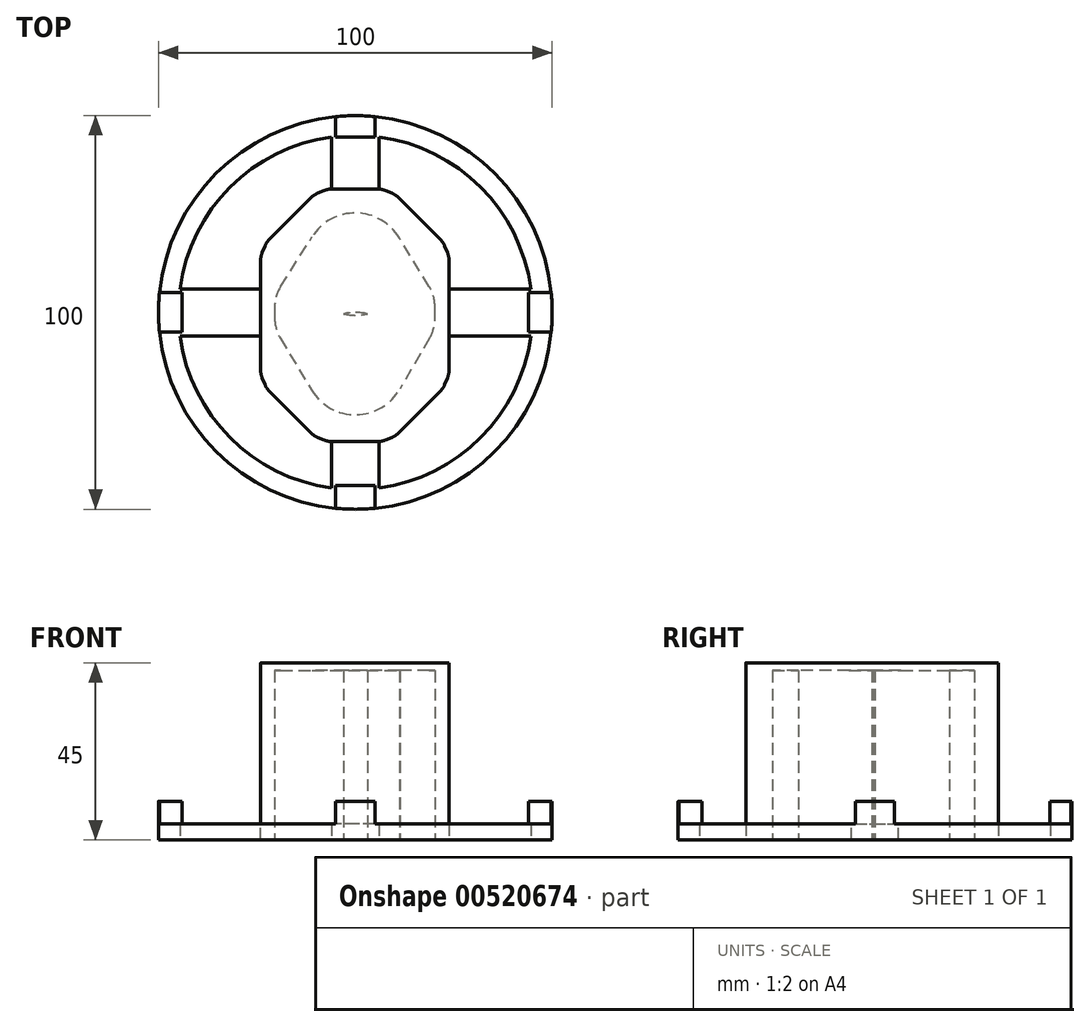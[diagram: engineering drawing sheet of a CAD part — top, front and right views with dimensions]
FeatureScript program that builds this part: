
annotation { "Feature Type Name" : "Feature", "Feature Type Description" : "" }
export const myFeature = defineFeature(function(context is Context, id is Id, definition is map)
    precondition{}
    {
        {
            var Q0;
            Q0=qCreatedBy(makeId("Top.planeOp"),FACE);
            var sketch = newSketch(context, id + "F0", { "sketchPlane" : qUnion([Q0])});
            skCircle(sketch, "E0", {"center": v(0, 0) * mm, "radius": 50 * mm});
            skSolve(sketch);
        }
        {
            var Q0;
            Q0=qSketchRegion(id+"F0",true);
            extrude(context, id + "F1", {"entities" : qUnion([Q0]), "depth" : 4 * mm, "offsetDistance" : 25 * mm});
        }
        {
            var Q0;
            Q0=makeQuery(id+"F1.opExtrude","CAP_FACE",FACE,{"disambiguationData":[OSD([sQuery(id+"F0.wireOp",EDGE,"E0")])],"isStart":false});
            var sketch = newSketch(context, id + "F2", { "sketchPlane" : qUnion([Q0])});
            skLineSegment(sketch, "E1.bottom", {"start": v(5, 50) * mm, "end": v(-5, 50) * mm});
            skLineSegment(sketch, "E1.top", {"start": v(5, 44.5) * mm, "end": v(-5, 44.5) * mm});
            skLineSegment(sketch, "E1.left", {"start": v(5, 50) * mm, "end": v(5, 44.5) * mm});
            skLineSegment(sketch, "E1.right", {"start": v(-5, 50) * mm, "end": v(-5, 44.5) * mm});
            skLineSegment(sketch, "E2.bottom", {"start": v(5, -44) * mm, "end": v(-5, -44) * mm});
            skLineSegment(sketch, "E2.top", {"start": v(5, -50) * mm, "end": v(-5, -50) * mm});
            skLineSegment(sketch, "E2.left", {"start": v(5, -44) * mm, "end": v(5, -50) * mm});
            skLineSegment(sketch, "E2.right", {"start": v(-5, -44) * mm, "end": v(-5, -50) * mm});
            skLineSegment(sketch, "E3.bottom", {"start": v(-44, 5) * mm, "end": v(-44, -5) * mm});
            skLineSegment(sketch, "E3.top", {"start": v(-50, 5) * mm, "end": v(-50, -5) * mm});
            skLineSegment(sketch, "E3.left", {"start": v(-50, 5) * mm, "end": v(-44, 5) * mm});
            skLineSegment(sketch, "E3.right", {"start": v(-50, -5) * mm, "end": v(-44, -5) * mm});
            skLineSegment(sketch, "E4.bottom", {"start": v(50, -5) * mm, "end": v(50, 5) * mm});
            skLineSegment(sketch, "E4.top", {"start": v(44, -5) * mm, "end": v(44, 5) * mm});
            skLineSegment(sketch, "E4.left", {"start": v(50, -5) * mm, "end": v(44, -5) * mm});
            skLineSegment(sketch, "E4.right", {"start": v(50, 5) * mm, "end": v(44, 5) * mm});
            skSolve(sketch);
        }
        {
            var Q0;
            {var subQ4=sQuery(id+"F2.wireOp",EDGE,"E1.top");Q0=makeQuery(id+"F2.imprint","IMPRINT",FACE,{"disambiguationData":[TD([[makeQuery(id+"F2.imprint","IMPRINT",EDGE,{"derivedFrom":subQ4}),-1.0]])]});}
            extrude(context, id + "F3", {"entities" : qUnion([Q0]), "operationType" : NewBodyOperationType.ADD, "depth" : 5.8 * mm, "offsetDistance" : 25 * mm});
        }
        {
            var Q0;
            {var subQ5=sQuery(id+"F2.wireOp",EDGE,"E2.bottom");Q0=makeQuery(id+"F2.imprint","IMPRINT",FACE,{"disambiguationData":[TD([[makeQuery(id+"F2.imprint","IMPRINT",EDGE,{"derivedFrom":subQ5}),1.0]])]});}
            extrude(context, id + "F4", {"entities" : qUnion([Q0]), "operationType" : NewBodyOperationType.ADD, "depth" : 5.8 * mm, "offsetDistance" : 25 * mm});
        }
        {
            var Q0;
            {var subQ5=sQuery(id+"F2.wireOp",EDGE,"E3.bottom");Q0=makeQuery(id+"F2.imprint","IMPRINT",FACE,{"disambiguationData":[TD([[makeQuery(id+"F2.imprint","IMPRINT",EDGE,{"derivedFrom":subQ5}),-1.0]])]});}
            var Q1;
            {var subQ1=sQuery(id+"F2.wireOp",EDGE,"E4.top");Q1=makeQuery(id+"F2.imprint","IMPRINT",FACE,{"disambiguationData":[TD([[makeQuery(id+"F2.imprint","IMPRINT",EDGE,{"derivedFrom":subQ1}),-1.0]])]});}
            extrude(context, id + "F5", {"entities" : qUnion([Q0, Q1]), "operationType" : NewBodyOperationType.ADD, "depth" : 5.8 * mm, "offsetDistance" : 25 * mm});
        }
        {
            var Q0;
            Q0=qCreatedBy(makeId("Top.planeOp"),FACE);
            var sketch = newSketch(context, id + "F6", { "sketchPlane" : qUnion([Q0])});
            skCircle(sketch, "E5", {"center": v(0, 0) * mm, "radius": 45 * mm});
            skSolve(sketch);
        }
        {
            var Q0;
            Q0=qSketchRegion(id+"F6",true);
            extrude(context, id + "F7", {"entities" : qUnion([Q0]), "operationType" : NewBodyOperationType.REMOVE, "depth" : 4 * mm, "offsetDistance" : 25 * mm});
        }
        {
            var Q0;
            Q0=qCreatedBy(makeId("Top.planeOp"),FACE);
            var sketch = newSketch(context, id + "F8", { "sketchPlane" : qUnion([Q0])});
            skLineSegment(sketch, "E6.bottom", {"start": v(-6, 46.88) * mm, "end": v(6, 46.88) * mm});
            skLineSegment(sketch, "E6.top", {"start": v(-6, 0) * mm, "end": v(6, 0) * mm});
            skLineSegment(sketch, "E6.left", {"start": v(-6, 46.88) * mm, "end": v(-6, 0) * mm});
            skLineSegment(sketch, "E6.right", {"start": v(6, 46.88) * mm, "end": v(6, 0) * mm});
            skLineSegment(sketch, "E7.top", {"start": v(-6, -46.78) * mm, "end": v(6, -46.78) * mm});
            skLineSegment(sketch, "E7.left", {"start": v(-6, 0) * mm, "end": v(-6, -46.78) * mm});
            skLineSegment(sketch, "E7.right", {"start": v(6, 0) * mm, "end": v(6, -46.78) * mm});
            skLineSegment(sketch, "E8.bottom", {"start": v(0, -6) * mm, "end": v(46.83, -6) * mm});
            skLineSegment(sketch, "E8.top", {"start": v(0, 6) * mm, "end": v(46.83, 6) * mm});
            skLineSegment(sketch, "E8.left", {"start": v(0, -6) * mm, "end": v(0, 6) * mm});
            skLineSegment(sketch, "E8.right", {"start": v(46.83, -6) * mm, "end": v(46.83, 6) * mm});
            skLineSegment(sketch, "E9.bottom", {"start": v(0, 6) * mm, "end": v(-46.57, 6) * mm});
            skLineSegment(sketch, "E9.top", {"start": v(0, -6) * mm, "end": v(-46.57, -6) * mm});
            skLineSegment(sketch, "E9.left", {"start": v(0, 6) * mm, "end": v(0, -6) * mm});
            skLineSegment(sketch, "E9.right", {"start": v(-46.57, 6) * mm, "end": v(-46.57, -6) * mm});
            skSolve(sketch);
        }
        {
            var Q0;
            Q0=qSketchRegion(id+"F8",true);
            extrude(context, id + "F9", {"entities" : qUnion([Q0]), "operationType" : NewBodyOperationType.ADD, "depth" : 4 * mm, "offsetDistance" : 25 * mm});
        }
        {
            var Q0;
            Q0=makeQuery(id+"FJTa6KurGkZYtoZ_1.boolean.opBoolean","MERGE",FACE,{"derivedFrom":[makeQuery(id+"F9.boolean.opBoolean","MERGE",FACE,{"derivedFrom":[makeQuery(id+"F1.opExtrude","CAP_FACE",FACE,{"disambiguationData":[OSD([sQuery(id+"F0.wireOp",EDGE,"E0")])],"isStart":true}),makeQuery(id+"F9.opExtrude","CAP_FACE",FACE,{"disambiguationData":[OSD([sQuery(id+"F8.wireOp",EDGE,"E6.bottom"),sQuery(id+"F8.wireOp",EDGE,"E6.left"),sQuery(id+"F8.wireOp",EDGE,"E6.right"),sQuery(id+"F8.wireOp",EDGE,"E7.top"),sQuery(id+"F8.wireOp",EDGE,"E7.left"),sQuery(id+"F8.wireOp",EDGE,"E7.right"),sQuery(id+"F8.wireOp",EDGE,"E8.bottom"),sQuery(id+"F8.wireOp",EDGE,"E8.top"),sQuery(id+"F8.wireOp",EDGE,"E8.right"),sQuery(id+"F8.wireOp",EDGE,"E9.bottom"),sQuery(id+"F8.wireOp",EDGE,"E9.top"),sQuery(id+"F8.wireOp",EDGE,"E9.right")])],"isStart":true})]}),makeQuery(id+"FJTa6KurGkZYtoZ_1.opExtrude","CAP_FACE",FACE,{"disambiguationData":[OSD([sQuery(id+"FEZX3pMElbrMIAv_1.wireOp",EDGE,"CWDysEy2-1OXt-7EfP-3vaQ-WOueIKtrEB2b")])],"isStart":true})]});
            var sketch = newSketch(context, id + "F10", { "sketchPlane" : qUnion([Q0])});
            skCircle(sketch, "E10", {"center": v(0, 0) * mm, "radius": 22.5 * mm});
            skSolve(sketch);
        }
        {
            var Q0;
            Q0=qSketchRegion(id+"F10",true);
            extrude(context, id + "F11", {"entities" : qUnion([Q0]), "operationType" : NewBodyOperationType.REMOVE, "oppositeDirection" : true, "depth" : 25 * mm, "offsetDistance" : 25 * mm});
        }
        {
            var Q0;
            Q0=qCreatedBy(makeId("Top.planeOp"),FACE);
            var sketch = newSketch(context, id + "F12", { "sketchPlane" : qUnion([Q0])});
            skLineSegment(sketch, "E11.bottom", {"start": v(-24.06, 31.35) * mm, "end": v(23.77, 31.35) * mm});
            skLineSegment(sketch, "E11.top", {"start": v(-24.06, -32.81) * mm, "end": v(23.77, -32.81) * mm});
            skLineSegment(sketch, "E11.left", {"start": v(-24.06, 31.35) * mm, "end": v(-24.06, -32.81) * mm});
            skLineSegment(sketch, "E11.right", {"start": v(23.77, 31.35) * mm, "end": v(23.77, -32.81) * mm});
            skSolve(sketch);
        }
        {
            var Q0;
            Q0 = qSketchRegion(id + "F12", true);
            extrude(context, id + "F13", {"entities" : qUnion([Q0]), "operationType" : NewBodyOperationType.ADD, "depth" : 45 * mm, "offsetDistance" : 25 * mm});
        }
        {
            var Q0;
            Q0=makeQuery(id+"F13.opExtrude","SWEPT_EDGE",EDGE,{"disambiguationData":[OSD([sQuery(id+"F12.wireOp",EDGE,"E11.bottom"),sQuery(id+"F12.wireOp",EDGE,"E11.left")])]});
            var Q1;
            Q1=makeQuery(id+"F13.opExtrude","SWEPT_EDGE",EDGE,{"disambiguationData":[OSD([sQuery(id+"F12.wireOp",EDGE,"E11.bottom"),sQuery(id+"F12.wireOp",EDGE,"E11.right")])]});
            var Q2;
            Q2=makeQuery(id+"F13.opExtrude","SWEPT_EDGE",EDGE,{"disambiguationData":[OSD([sQuery(id+"F12.wireOp",EDGE,"E11.top"),sQuery(id+"F12.wireOp",EDGE,"E11.right")])]});
            var Q3;
            Q3=makeQuery(id+"F13.opExtrude","SWEPT_EDGE",EDGE,{"disambiguationData":[OSD([sQuery(id+"F12.wireOp",EDGE,"E11.top"),sQuery(id+"F12.wireOp",EDGE,"E11.left")])]});
            chamfer(context, id + "F14", {"entities" : qUnion([Q0, Q1, Q2, Q3]), "width" : 15 * mm, "tangentPropagation" : true});
        }
        {
            var Q0;
            {var subQ0=sQuery(id+"F12.wireOp",EDGE,"E11.bottom");Q0=makeQuery(id+"F14.opChamfer","BLEND_EDGE",EDGE,{"blendedFrom":[makeQuery(id+"F13.opExtrude","SWEPT_EDGE",EDGE,{"disambiguationData":[OSD([subQ0,sQuery(id+"F12.wireOp",EDGE,"E11.left")])]}),makeQuery(id+"F13.opExtrude","SWEPT_FACE",FACE,{"disambiguationData":[OSD([subQ0])]})],"blendedInto":[makeQuery(id+"F13.opExtrude","SWEPT_FACE",FACE,{"disambiguationData":[OSD([subQ0])]})]});}
            var Q1;
            {var subQ0=sQuery(id+"F12.wireOp",EDGE,"E11.bottom");Q1=makeQuery(id+"F14.opChamfer","BLEND_EDGE",EDGE,{"blendedFrom":[makeQuery(id+"F13.opExtrude","SWEPT_EDGE",EDGE,{"disambiguationData":[OSD([subQ0,sQuery(id+"F12.wireOp",EDGE,"E11.right")])]}),makeQuery(id+"F13.opExtrude","SWEPT_FACE",FACE,{"disambiguationData":[OSD([subQ0])]})],"blendedInto":[makeQuery(id+"F13.opExtrude","SWEPT_FACE",FACE,{"disambiguationData":[OSD([subQ0])]})]});}
            var Q2;
            {var subQ0=sQuery(id+"F12.wireOp",EDGE,"E11.left");Q2=makeQuery(id+"F14.opChamfer","BLEND_EDGE",EDGE,{"blendedFrom":[makeQuery(id+"F13.opExtrude","SWEPT_EDGE",EDGE,{"disambiguationData":[OSD([sQuery(id+"F12.wireOp",EDGE,"E11.top"),subQ0])]}),makeQuery(id+"F13.opExtrude","SWEPT_FACE",FACE,{"disambiguationData":[OSD([subQ0])]})],"blendedInto":[makeQuery(id+"F13.opExtrude","SWEPT_FACE",FACE,{"disambiguationData":[OSD([subQ0])]})]});}
            var Q3;
            {var subQ0=sQuery(id+"F12.wireOp",EDGE,"E11.top");Q3=makeQuery(id+"F14.opChamfer","BLEND_EDGE",EDGE,{"blendedFrom":[makeQuery(id+"F13.opExtrude","SWEPT_EDGE",EDGE,{"disambiguationData":[OSD([subQ0,sQuery(id+"F12.wireOp",EDGE,"E11.left")])]}),makeQuery(id+"F13.opExtrude","SWEPT_FACE",FACE,{"disambiguationData":[OSD([subQ0])]})],"blendedInto":[makeQuery(id+"F13.opExtrude","SWEPT_FACE",FACE,{"disambiguationData":[OSD([subQ0])]})]});}
            var Q4;
            {var subQ0=sQuery(id+"F12.wireOp",EDGE,"E11.top");Q4=makeQuery(id+"F14.opChamfer","BLEND_EDGE",EDGE,{"blendedFrom":[makeQuery(id+"F13.opExtrude","SWEPT_EDGE",EDGE,{"disambiguationData":[OSD([subQ0,sQuery(id+"F12.wireOp",EDGE,"E11.right")])]}),makeQuery(id+"F13.opExtrude","SWEPT_FACE",FACE,{"disambiguationData":[OSD([subQ0])]})],"blendedInto":[makeQuery(id+"F13.opExtrude","SWEPT_FACE",FACE,{"disambiguationData":[OSD([subQ0])]})]});}
            var Q5;
            {var subQ0=sQuery(id+"F12.wireOp",EDGE,"E11.right");Q5=makeQuery(id+"F14.opChamfer","BLEND_EDGE",EDGE,{"blendedFrom":[makeQuery(id+"F13.opExtrude","SWEPT_EDGE",EDGE,{"disambiguationData":[OSD([sQuery(id+"F12.wireOp",EDGE,"E11.top"),subQ0])]}),makeQuery(id+"F13.opExtrude","SWEPT_FACE",FACE,{"disambiguationData":[OSD([subQ0])]})],"blendedInto":[makeQuery(id+"F13.opExtrude","SWEPT_FACE",FACE,{"disambiguationData":[OSD([subQ0])]})]});}
            var Q6;
            {var subQ0=sQuery(id+"F12.wireOp",EDGE,"E11.right");Q6=makeQuery(id+"F14.opChamfer","BLEND_EDGE",EDGE,{"blendedFrom":[makeQuery(id+"F13.opExtrude","SWEPT_EDGE",EDGE,{"disambiguationData":[OSD([sQuery(id+"F12.wireOp",EDGE,"E11.bottom"),subQ0])]}),makeQuery(id+"F13.opExtrude","SWEPT_FACE",FACE,{"disambiguationData":[OSD([subQ0])]})],"blendedInto":[makeQuery(id+"F13.opExtrude","SWEPT_FACE",FACE,{"disambiguationData":[OSD([subQ0])]})]});}
            var Q7;
            {var subQ0=sQuery(id+"F12.wireOp",EDGE,"E11.left");Q7=makeQuery(id+"F14.opChamfer","BLEND_EDGE",EDGE,{"blendedFrom":[makeQuery(id+"F13.opExtrude","SWEPT_EDGE",EDGE,{"disambiguationData":[OSD([sQuery(id+"F12.wireOp",EDGE,"E11.bottom"),subQ0])]}),makeQuery(id+"F13.opExtrude","SWEPT_FACE",FACE,{"disambiguationData":[OSD([subQ0])]})],"blendedInto":[makeQuery(id+"F13.opExtrude","SWEPT_FACE",FACE,{"disambiguationData":[OSD([subQ0])]})]});}
            chamfer(context, id + "F15", {"entities" : qUnion([Q0, Q1, Q2, Q3, Q4, Q5, Q6, Q7]), "width" : 5 * mm, "tangentPropagation" : true});
        }
        {
            var Q0;
            {var subQ0=sQuery(id+"F12.wireOp",EDGE,"E11.left");var subQ1=makeQuery(id+"F13.opExtrude","SWEPT_FACE",FACE,{"disambiguationData":[OSD([subQ0])]});Q0=makeQuery(id+"F15.opChamfer","BLEND_EDGE",EDGE,{"blendedFrom":[makeQuery(id+"F14.opChamfer","BLEND_EDGE",EDGE,{"blendedFrom":[makeQuery(id+"F13.opExtrude","SWEPT_EDGE",EDGE,{"disambiguationData":[OSD([sQuery(id+"F12.wireOp",EDGE,"E11.bottom"),subQ0])]}),subQ1],"blendedInto":[subQ1]}),subQ1],"blendedInto":[subQ1]});}
            var Q1;
            {var subQ0=sQuery(id+"F12.wireOp",EDGE,"E11.left");var subQ1=sQuery(id+"F12.wireOp",EDGE,"E11.bottom");Q1=makeQuery(id+"F15.opChamfer","BLEND_EDGE",EDGE,{"blendedFrom":[makeQuery(id+"F14.opChamfer","BLEND_EDGE",EDGE,{"blendedFrom":[makeQuery(id+"F13.opExtrude","SWEPT_EDGE",EDGE,{"disambiguationData":[OSD([subQ1,subQ0])]}),makeQuery(id+"F13.opExtrude","SWEPT_FACE",FACE,{"disambiguationData":[OSD([subQ0])]})],"blendedInto":[makeQuery(id+"F13.opExtrude","SWEPT_FACE",FACE,{"disambiguationData":[OSD([subQ0])]})]}),makeQuery(id+"F14.opChamfer","BLEND_FACE",FACE,{"disambiguationData":[OSD([subQ1,subQ0])]})],"blendedInto":[makeQuery(id+"F14.opChamfer","BLEND_FACE",FACE,{"disambiguationData":[OSD([subQ1,subQ0])]})]});}
            var Q2;
            {var subQ0=sQuery(id+"F12.wireOp",EDGE,"E11.left");var subQ1=sQuery(id+"F12.wireOp",EDGE,"E11.bottom");Q2=makeQuery(id+"F15.opChamfer","BLEND_EDGE",EDGE,{"blendedFrom":[makeQuery(id+"F14.opChamfer","BLEND_EDGE",EDGE,{"blendedFrom":[makeQuery(id+"F13.opExtrude","SWEPT_EDGE",EDGE,{"disambiguationData":[OSD([subQ1,subQ0])]}),makeQuery(id+"F13.opExtrude","SWEPT_FACE",FACE,{"disambiguationData":[OSD([subQ1])]})],"blendedInto":[makeQuery(id+"F13.opExtrude","SWEPT_FACE",FACE,{"disambiguationData":[OSD([subQ1])]})]}),makeQuery(id+"F14.opChamfer","BLEND_FACE",FACE,{"disambiguationData":[OSD([subQ1,subQ0])]})],"blendedInto":[makeQuery(id+"F14.opChamfer","BLEND_FACE",FACE,{"disambiguationData":[OSD([subQ1,subQ0])]})]});}
            var Q3;
            {var subQ0=sQuery(id+"F12.wireOp",EDGE,"E11.bottom");var subQ1=makeQuery(id+"F13.opExtrude","SWEPT_FACE",FACE,{"disambiguationData":[OSD([subQ0])]});Q3=makeQuery(id+"F15.opChamfer","BLEND_EDGE",EDGE,{"blendedFrom":[makeQuery(id+"F14.opChamfer","BLEND_EDGE",EDGE,{"blendedFrom":[makeQuery(id+"F13.opExtrude","SWEPT_EDGE",EDGE,{"disambiguationData":[OSD([subQ0,sQuery(id+"F12.wireOp",EDGE,"E11.left")])]}),subQ1],"blendedInto":[subQ1]}),subQ1],"blendedInto":[subQ1]});}
            var Q4;
            {var subQ0=sQuery(id+"F12.wireOp",EDGE,"E11.bottom");var subQ1=makeQuery(id+"F13.opExtrude","SWEPT_FACE",FACE,{"disambiguationData":[OSD([subQ0])]});Q4=makeQuery(id+"F15.opChamfer","BLEND_EDGE",EDGE,{"blendedFrom":[makeQuery(id+"F14.opChamfer","BLEND_EDGE",EDGE,{"blendedFrom":[makeQuery(id+"F13.opExtrude","SWEPT_EDGE",EDGE,{"disambiguationData":[OSD([subQ0,sQuery(id+"F12.wireOp",EDGE,"E11.right")])]}),subQ1],"blendedInto":[subQ1]}),subQ1],"blendedInto":[subQ1]});}
            var Q5;
            {var subQ0=sQuery(id+"F12.wireOp",EDGE,"E11.right");var subQ1=sQuery(id+"F12.wireOp",EDGE,"E11.bottom");Q5=makeQuery(id+"F15.opChamfer","BLEND_EDGE",EDGE,{"blendedFrom":[makeQuery(id+"F14.opChamfer","BLEND_EDGE",EDGE,{"blendedFrom":[makeQuery(id+"F13.opExtrude","SWEPT_EDGE",EDGE,{"disambiguationData":[OSD([subQ1,subQ0])]}),makeQuery(id+"F13.opExtrude","SWEPT_FACE",FACE,{"disambiguationData":[OSD([subQ1])]})],"blendedInto":[makeQuery(id+"F13.opExtrude","SWEPT_FACE",FACE,{"disambiguationData":[OSD([subQ1])]})]}),makeQuery(id+"F14.opChamfer","BLEND_FACE",FACE,{"disambiguationData":[OSD([subQ1,subQ0])]})],"blendedInto":[makeQuery(id+"F14.opChamfer","BLEND_FACE",FACE,{"disambiguationData":[OSD([subQ1,subQ0])]})]});}
            var Q6;
            {var subQ0=sQuery(id+"F12.wireOp",EDGE,"E11.right");var subQ1=sQuery(id+"F12.wireOp",EDGE,"E11.bottom");Q6=makeQuery(id+"F15.opChamfer","BLEND_EDGE",EDGE,{"blendedFrom":[makeQuery(id+"F14.opChamfer","BLEND_EDGE",EDGE,{"blendedFrom":[makeQuery(id+"F13.opExtrude","SWEPT_EDGE",EDGE,{"disambiguationData":[OSD([subQ1,subQ0])]}),makeQuery(id+"F13.opExtrude","SWEPT_FACE",FACE,{"disambiguationData":[OSD([subQ0])]})],"blendedInto":[makeQuery(id+"F13.opExtrude","SWEPT_FACE",FACE,{"disambiguationData":[OSD([subQ0])]})]}),makeQuery(id+"F14.opChamfer","BLEND_FACE",FACE,{"disambiguationData":[OSD([subQ1,subQ0])]})],"blendedInto":[makeQuery(id+"F14.opChamfer","BLEND_FACE",FACE,{"disambiguationData":[OSD([subQ1,subQ0])]})]});}
            var Q7;
            {var subQ0=sQuery(id+"F12.wireOp",EDGE,"E11.right");var subQ1=makeQuery(id+"F13.opExtrude","SWEPT_FACE",FACE,{"disambiguationData":[OSD([subQ0])]});Q7=makeQuery(id+"F15.opChamfer","BLEND_EDGE",EDGE,{"blendedFrom":[makeQuery(id+"F14.opChamfer","BLEND_EDGE",EDGE,{"blendedFrom":[makeQuery(id+"F13.opExtrude","SWEPT_EDGE",EDGE,{"disambiguationData":[OSD([sQuery(id+"F12.wireOp",EDGE,"E11.bottom"),subQ0])]}),subQ1],"blendedInto":[subQ1]}),subQ1],"blendedInto":[subQ1]});}
            var Q8;
            {var subQ0=sQuery(id+"F12.wireOp",EDGE,"E11.right");var subQ1=makeQuery(id+"F13.opExtrude","SWEPT_FACE",FACE,{"disambiguationData":[OSD([subQ0])]});Q8=makeQuery(id+"F15.opChamfer","BLEND_EDGE",EDGE,{"blendedFrom":[makeQuery(id+"F14.opChamfer","BLEND_EDGE",EDGE,{"blendedFrom":[makeQuery(id+"F13.opExtrude","SWEPT_EDGE",EDGE,{"disambiguationData":[OSD([sQuery(id+"F12.wireOp",EDGE,"E11.top"),subQ0])]}),subQ1],"blendedInto":[subQ1]}),subQ1],"blendedInto":[subQ1]});}
            var Q9;
            {var subQ0=sQuery(id+"F12.wireOp",EDGE,"E11.right");var subQ1=sQuery(id+"F12.wireOp",EDGE,"E11.top");Q9=makeQuery(id+"F15.opChamfer","BLEND_EDGE",EDGE,{"blendedFrom":[makeQuery(id+"F14.opChamfer","BLEND_EDGE",EDGE,{"blendedFrom":[makeQuery(id+"F13.opExtrude","SWEPT_EDGE",EDGE,{"disambiguationData":[OSD([subQ1,subQ0])]}),makeQuery(id+"F13.opExtrude","SWEPT_FACE",FACE,{"disambiguationData":[OSD([subQ0])]})],"blendedInto":[makeQuery(id+"F13.opExtrude","SWEPT_FACE",FACE,{"disambiguationData":[OSD([subQ0])]})]}),makeQuery(id+"F14.opChamfer","BLEND_FACE",FACE,{"disambiguationData":[OSD([subQ1,subQ0])]})],"blendedInto":[makeQuery(id+"F14.opChamfer","BLEND_FACE",FACE,{"disambiguationData":[OSD([subQ1,subQ0])]})]});}
            var Q10;
            {var subQ0=sQuery(id+"F12.wireOp",EDGE,"E11.right");var subQ1=sQuery(id+"F12.wireOp",EDGE,"E11.top");Q10=makeQuery(id+"F15.opChamfer","BLEND_EDGE",EDGE,{"blendedFrom":[makeQuery(id+"F14.opChamfer","BLEND_EDGE",EDGE,{"blendedFrom":[makeQuery(id+"F13.opExtrude","SWEPT_EDGE",EDGE,{"disambiguationData":[OSD([subQ1,subQ0])]}),makeQuery(id+"F13.opExtrude","SWEPT_FACE",FACE,{"disambiguationData":[OSD([subQ1])]})],"blendedInto":[makeQuery(id+"F13.opExtrude","SWEPT_FACE",FACE,{"disambiguationData":[OSD([subQ1])]})]}),makeQuery(id+"F14.opChamfer","BLEND_FACE",FACE,{"disambiguationData":[OSD([subQ1,subQ0])]})],"blendedInto":[makeQuery(id+"F14.opChamfer","BLEND_FACE",FACE,{"disambiguationData":[OSD([subQ1,subQ0])]})]});}
            var Q11;
            {var subQ0=sQuery(id+"F12.wireOp",EDGE,"E11.top");var subQ1=makeQuery(id+"F13.opExtrude","SWEPT_FACE",FACE,{"disambiguationData":[OSD([subQ0])]});Q11=makeQuery(id+"F15.opChamfer","BLEND_EDGE",EDGE,{"blendedFrom":[makeQuery(id+"F14.opChamfer","BLEND_EDGE",EDGE,{"blendedFrom":[makeQuery(id+"F13.opExtrude","SWEPT_EDGE",EDGE,{"disambiguationData":[OSD([subQ0,sQuery(id+"F12.wireOp",EDGE,"E11.right")])]}),subQ1],"blendedInto":[subQ1]}),subQ1],"blendedInto":[subQ1]});}
            var Q12;
            {var subQ0=sQuery(id+"F12.wireOp",EDGE,"E11.top");var subQ1=makeQuery(id+"F13.opExtrude","SWEPT_FACE",FACE,{"disambiguationData":[OSD([subQ0])]});Q12=makeQuery(id+"F15.opChamfer","BLEND_EDGE",EDGE,{"blendedFrom":[makeQuery(id+"F14.opChamfer","BLEND_EDGE",EDGE,{"blendedFrom":[makeQuery(id+"F13.opExtrude","SWEPT_EDGE",EDGE,{"disambiguationData":[OSD([subQ0,sQuery(id+"F12.wireOp",EDGE,"E11.left")])]}),subQ1],"blendedInto":[subQ1]}),subQ1],"blendedInto":[subQ1]});}
            var Q13;
            {var subQ0=sQuery(id+"F12.wireOp",EDGE,"E11.left");var subQ1=makeQuery(id+"F13.opExtrude","SWEPT_FACE",FACE,{"disambiguationData":[OSD([subQ0])]});Q13=makeQuery(id+"F15.opChamfer","BLEND_EDGE",EDGE,{"blendedFrom":[makeQuery(id+"F14.opChamfer","BLEND_EDGE",EDGE,{"blendedFrom":[makeQuery(id+"F13.opExtrude","SWEPT_EDGE",EDGE,{"disambiguationData":[OSD([sQuery(id+"F12.wireOp",EDGE,"E11.top"),subQ0])]}),subQ1],"blendedInto":[subQ1]}),subQ1],"blendedInto":[subQ1]});}
            var Q14;
            {var subQ0=sQuery(id+"F12.wireOp",EDGE,"E11.left");var subQ1=sQuery(id+"F12.wireOp",EDGE,"E11.top");Q14=makeQuery(id+"F15.opChamfer","BLEND_EDGE",EDGE,{"blendedFrom":[makeQuery(id+"F14.opChamfer","BLEND_EDGE",EDGE,{"blendedFrom":[makeQuery(id+"F13.opExtrude","SWEPT_EDGE",EDGE,{"disambiguationData":[OSD([subQ1,subQ0])]}),makeQuery(id+"F13.opExtrude","SWEPT_FACE",FACE,{"disambiguationData":[OSD([subQ0])]})],"blendedInto":[makeQuery(id+"F13.opExtrude","SWEPT_FACE",FACE,{"disambiguationData":[OSD([subQ0])]})]}),makeQuery(id+"F14.opChamfer","BLEND_FACE",FACE,{"disambiguationData":[OSD([subQ1,subQ0])]})],"blendedInto":[makeQuery(id+"F14.opChamfer","BLEND_FACE",FACE,{"disambiguationData":[OSD([subQ1,subQ0])]})]});}
            var Q15;
            {var subQ0=sQuery(id+"F12.wireOp",EDGE,"E11.left");var subQ1=sQuery(id+"F12.wireOp",EDGE,"E11.top");Q15=makeQuery(id+"F15.opChamfer","BLEND_EDGE",EDGE,{"blendedFrom":[makeQuery(id+"F14.opChamfer","BLEND_EDGE",EDGE,{"blendedFrom":[makeQuery(id+"F13.opExtrude","SWEPT_EDGE",EDGE,{"disambiguationData":[OSD([subQ1,subQ0])]}),makeQuery(id+"F13.opExtrude","SWEPT_FACE",FACE,{"disambiguationData":[OSD([subQ1])]})],"blendedInto":[makeQuery(id+"F13.opExtrude","SWEPT_FACE",FACE,{"disambiguationData":[OSD([subQ1])]})]}),makeQuery(id+"F14.opChamfer","BLEND_FACE",FACE,{"disambiguationData":[OSD([subQ1,subQ0])]})],"blendedInto":[makeQuery(id+"F14.opChamfer","BLEND_FACE",FACE,{"disambiguationData":[OSD([subQ1,subQ0])]})]});}
            fillet(context, id + "F16", {"entities" : qUnion([Q0, Q1, Q2, Q3, Q4, Q5, Q6, Q7, Q8, Q9, Q10, Q11, Q12, Q13, Q14, Q15]), "radius" : 5 * mm, "tangentPropagation" : true, "allowEdgeOverflow" : false});
        }
        {
            var Q0;
            Q0=makeQuery(id+"F13.boolean.opBoolean","MERGE",FACE,{"derivedFrom":[makeQuery(id+"F9.boolean.opBoolean","MERGE",FACE,{"derivedFrom":[makeQuery(id+"F1.opExtrude","CAP_FACE",FACE,{"disambiguationData":[OSD([sQuery(id+"F0.wireOp",EDGE,"E0")])],"isStart":true}),makeQuery(id+"F9.opExtrude","CAP_FACE",FACE,{"disambiguationData":[OSD([sQuery(id+"F8.wireOp",EDGE,"E6.bottom"),sQuery(id+"F8.wireOp",EDGE,"E6.left"),sQuery(id+"F8.wireOp",EDGE,"E6.right"),sQuery(id+"F8.wireOp",EDGE,"E7.top"),sQuery(id+"F8.wireOp",EDGE,"E7.left"),sQuery(id+"F8.wireOp",EDGE,"E7.right"),sQuery(id+"F8.wireOp",EDGE,"E8.bottom"),sQuery(id+"F8.wireOp",EDGE,"E8.top"),sQuery(id+"F8.wireOp",EDGE,"E8.right"),sQuery(id+"F8.wireOp",EDGE,"E9.bottom"),sQuery(id+"F8.wireOp",EDGE,"E9.top"),sQuery(id+"F8.wireOp",EDGE,"E9.right")])],"isStart":true})]}),makeQuery(id+"F13.opExtrude","CAP_FACE",FACE,{"disambiguationData":[OSD([sQuery(id+"F12.wireOp",EDGE,"E11.bottom"),sQuery(id+"F12.wireOp",EDGE,"E11.top"),sQuery(id+"F12.wireOp",EDGE,"E11.left"),sQuery(id+"F12.wireOp",EDGE,"E11.right")])],"isStart":true})]});
            var sketch = newSketch(context, id + "F17", { "sketchPlane" : qUnion([Q0])});
            skCircle(sketch, "E12", {"center": v(0, 13) * mm, "radius": 13 * mm});
            skCircle(sketch, "E13", {"center": v(0, -12.27) * mm, "radius": 13 * mm});
            skLineSegment(sketch, "E14", {"start": v(-20.5, -4.18) * mm, "end": v(-20.5, 4.18) * mm});
            skLineSegment(sketch, "E15", {"start": v(-20.5, 4.18) * mm, "end": v(-11.13, 19.71) * mm});
            skLineSegment(sketch, "E16", {"start": v(-20.5, -4.18) * mm, "end": v(-10.99, -19.22) * mm});
            skLineSegment(sketch, "E17", {"start": v(20.2, 4.18) * mm, "end": v(11.13, 19.71) * mm});
            skLineSegment(sketch, "E18", {"start": v(11.13, 19.71) * mm, "end": v(20.2, 4.18) * mm});
            skLineSegment(sketch, "E19", {"start": v(20.2, -4.18) * mm, "end": v(10.99, -19.22) * mm});
            skLineSegment(sketch, "E20", {"start": v(10.99, -19.22) * mm, "end": v(20.2, -4.18) * mm});
            skLineSegment(sketch, "E21", {"start": v(20.2, 4.18) * mm, "end": v(20.2, -4.18) * mm});
            skSolve(sketch);
        }
        {
            var Q0;
            Q0 = qSketchRegion(id + "F17", true);
            var Q1;
            {var subQ0=sQuery(id+"F17.wireOp",EDGE,"E13");var subQ1=sQuery(id+"F17.wireOp",EDGE,"E12");var subQ2=makeQuery(id+"F17.imprint","INTERSECT",VERTEX,{"disambiguationData":[OD(0.0)],"derivedFrom":[subQ1,subQ0]});Q1=makeQuery(id+"F17.imprint","IMPRINT",FACE,{"disambiguationData":[TD([[makeQuery(id+"F17.imprint","IMPRINT",EDGE,{"disambiguationData":[TD([[subQ2,-1.0]])],"derivedFrom":subQ1}),1.0]])]});}
            extrude(context, id + "F18", {"entities" : qUnion([Q0, Q1]), "operationType" : NewBodyOperationType.REMOVE, "oppositeDirection" : true, "depth" : 43 * mm, "offsetDistance" : 25 * mm});
        }
        {
            var Q0;
            Q0=makeQuery(id+"F18.boolean.opBoolean","COPY",EDGE,{"derivedFrom":makeQuery(id+"F18.opExtrude","SWEPT_EDGE",EDGE,{"disambiguationData":[OSD([sQuery(id+"F17.wireOp",EDGE,"E14"),sQuery(id+"F17.wireOp",EDGE,"E16")])]})});
            var Q1;
            Q1=makeQuery(id+"F18.boolean.opBoolean","COPY",EDGE,{"derivedFrom":makeQuery(id+"F18.opExtrude","SWEPT_EDGE",EDGE,{"disambiguationData":[OSD([sQuery(id+"F17.wireOp",EDGE,"E20"),sQuery(id+"F17.wireOp",EDGE,"E21")])]})});
            var Q2;
            Q2=makeQuery(id+"F18.boolean.opBoolean","COPY",EDGE,{"derivedFrom":makeQuery(id+"F18.opExtrude","SWEPT_EDGE",EDGE,{"disambiguationData":[OSD([sQuery(id+"F17.wireOp",EDGE,"E14"),sQuery(id+"F17.wireOp",EDGE,"E15")])]})});
            var Q3;
            Q3=makeQuery(id+"F18.boolean.opBoolean","COPY",EDGE,{"derivedFrom":makeQuery(id+"F18.opExtrude","SWEPT_EDGE",EDGE,{"disambiguationData":[OSD([sQuery(id+"F17.wireOp",EDGE,"E18"),sQuery(id+"F17.wireOp",EDGE,"E21")])]})});
            fillet(context, id + "F19", {"entities" : qUnion([Q0, Q1, Q2, Q3]), "radius" : 10 * mm, "tangentPropagation" : true, "allowEdgeOverflow" : false});
        }
    });
